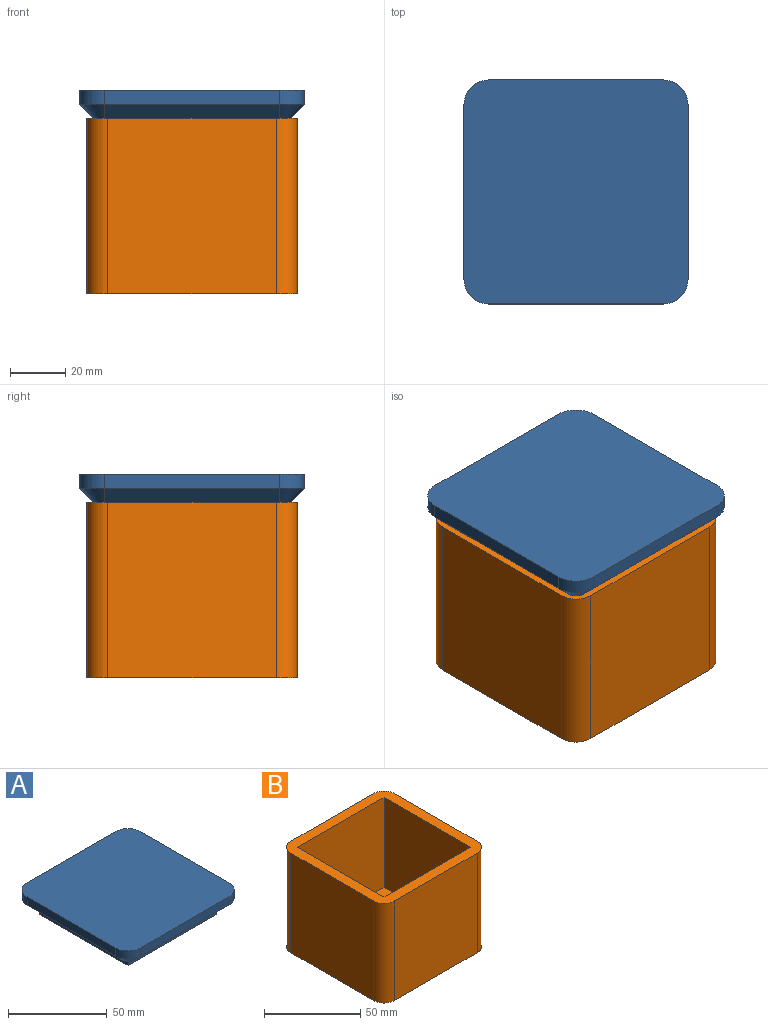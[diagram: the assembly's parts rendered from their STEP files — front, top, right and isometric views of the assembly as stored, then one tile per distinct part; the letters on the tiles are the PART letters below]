
ASSEMBLY  parts=2 mates=1
PART A: 28 faces, bbox 81.3x81.3x15.2 mm
  f0: plane 63.5x63.5mm, normal (0,0,-1), area 1187.1mm2, adj f7,f8,f9,f10,f11,f12,f13,f14
  f1: plane 63.5x5.08mm, normal (-1,0,0), area 322.6mm2, adj f5,f16,f19,f23
  f2: plane 63.5x5.08mm, normal (0,-1,0), area 322.6mm2, adj f5,f16,f17,f20
  f3: plane 63.5x5.08mm, normal (1,0,0), area 322.6mm2, adj f5,f17,f18,f24
  f4: plane 63.5x5.08mm, normal (0,1,0), area 322.6mm2, adj f5,f18,f19,f27
  f5: plane 81.28x81.28mm, normal (0,0,1), area 6538.6mm2, adj f1,f2,f3,f4,f16,f17,f18,f19
  f6: plane 71.12x71.12mm, normal (0,0,-1), area 1013.3mm2, adj f7,f8,f9,f10,f20,f21,f22,f23
  f7: plane 63.5x5.08mm, normal (-1,0,0), area 322.6mm2, adj f0,f6,f8,f10
  f8: plane 63.5x5.08mm, normal (0,1,0), area 322.6mm2, adj f0,f6,f7,f9
  f9: plane 63.5x5.08mm, normal (1,0,0), area 322.6mm2, adj f0,f6,f8,f10
  f10: plane 63.5x5.08mm, normal (0,-1,0), area 322.6mm2, adj f0,f6,f7,f9
  f11: plane 53.34x5.08mm, normal (1,0,0), area 271mm2, adj f0,f12,f14,f15
  f12: plane 53.34x5.08mm, normal (0,-1,0), area 271mm2, adj f0,f11,f13,f15
  f13: plane 53.34x5.08mm, normal (-1,0,0), area 271mm2, adj f0,f12,f14,f15
  f14: plane 53.34x5.08mm, normal (0,1,0), area 271mm2, adj f0,f11,f13,f15
  f15: plane 53.34x53.34mm, normal (0,0,-1), area 2845.2mm2, adj f11,f12,f13,f14
  f16: cylinder r=8.89mm len=8.89mm, axis (0,0,1), area 70.9mm2, adj f1,f2,f5,f21
  f17: cylinder r=8.89mm len=8.89mm, axis (0,0,-1), area 70.9mm2, adj f2,f3,f5,f22
  f18: cylinder r=8.89mm len=8.89mm, axis (0,0,1), area 70.9mm2, adj f3,f4,f5,f26
  f19: cylinder r=8.89mm len=8.89mm, axis (0,0,-1), area 70.9mm2, adj f1,f4,f5,f25
  f20: plane 63.5x5.08mm, normal (0,-0.71,-0.71), area 456.2mm2, adj f2,f6,f21,f22
  f21: cone r=3.81mm half-angle=45deg, axis (0,0,1), area 71.7mm2, adj f6,f16,f20,f23
  f22: cone r=3.81mm half-angle=45deg, axis (0,0,1), area 71.7mm2, adj f6,f17,f20,f24
  f23: plane 63.5x5.08mm, normal (-0.71,0,-0.71), area 456.2mm2, adj f1,f6,f21,f25
  f24: plane 63.5x5.08mm, normal (0.71,0,-0.71), area 456.2mm2, adj f3,f6,f22,f26
  f25: cone r=3.81mm half-angle=45deg, axis (0,0,1), area 71.7mm2, adj f6,f19,f23,f27
  f26: cone r=3.81mm half-angle=45deg, axis (0,0,1), area 71.7mm2, adj f6,f18,f24,f27
  f27: plane 63.5x5.08mm, normal (0,0.71,-0.71), area 456.2mm2, adj f4,f6,f25,f26
PART B: 15 faces, bbox 76.2x76.2x63.5 mm
  f0: plane 76.2x76.2mm, normal (0,0,1), area 1724.3mm2, adj f1,f2,f3,f4,f6,f7,f8,f9
  f1: plane 63.5x60.96mm, normal (-1,0,0), area 3871mm2, adj f0,f5,f11,f14
  f2: plane 63.5x60.96mm, normal (0,-1,0), area 3871mm2, adj f0,f5,f11,f12
  f3: plane 63.5x60.96mm, normal (1,0,0), area 3871mm2, adj f0,f5,f12,f13
  f4: plane 63.5x60.96mm, normal (0,1,0), area 3871mm2, adj f0,f5,f13,f14
  f5: plane 76.2x76.2mm, normal (0,0,-1), area 5756.6mm2, adj f1,f2,f3,f4,f11,f12,f13,f14
  f6: plane 63.5x57.4mm, normal (1,0,0), area 3645.2mm2, adj f0,f7,f9,f10
  f7: plane 63.5x57.4mm, normal (0,1,0), area 3645.2mm2, adj f0,f6,f8,f10
  f8: plane 63.5x57.4mm, normal (-1,0,0), area 3645.2mm2, adj f0,f7,f9,f10
  f9: plane 63.5x57.4mm, normal (0,-1,0), area 3645.2mm2, adj f0,f6,f8,f10
  f10: plane 63.5x63.5mm, normal (0,0,1), area 4032.3mm2, adj f6,f7,f8,f9
  f11: cylinder r=7.62mm len=63.5mm, axis (0,0,1), area 760.1mm2, adj f0,f1,f2,f5
  f12: cylinder r=7.62mm len=63.5mm, axis (0,0,-1), area 760.1mm2, adj f0,f2,f3,f5
  f13: cylinder r=7.62mm len=63.5mm, axis (0,0,1), area 760.1mm2, adj f0,f3,f4,f5
  f14: cylinder r=7.62mm len=63.5mm, axis (0,0,-1), area 760.1mm2, adj f0,f1,f4,f5
PLACE A t=(140.75,-16.51,-118.62)mm
PLACE B t=(0,-16.51,-182.12)mm
MATE slider A.f16 <-> B.f0  axis (0,0,1) through (-31.75,-48.26,-123.7)mm
